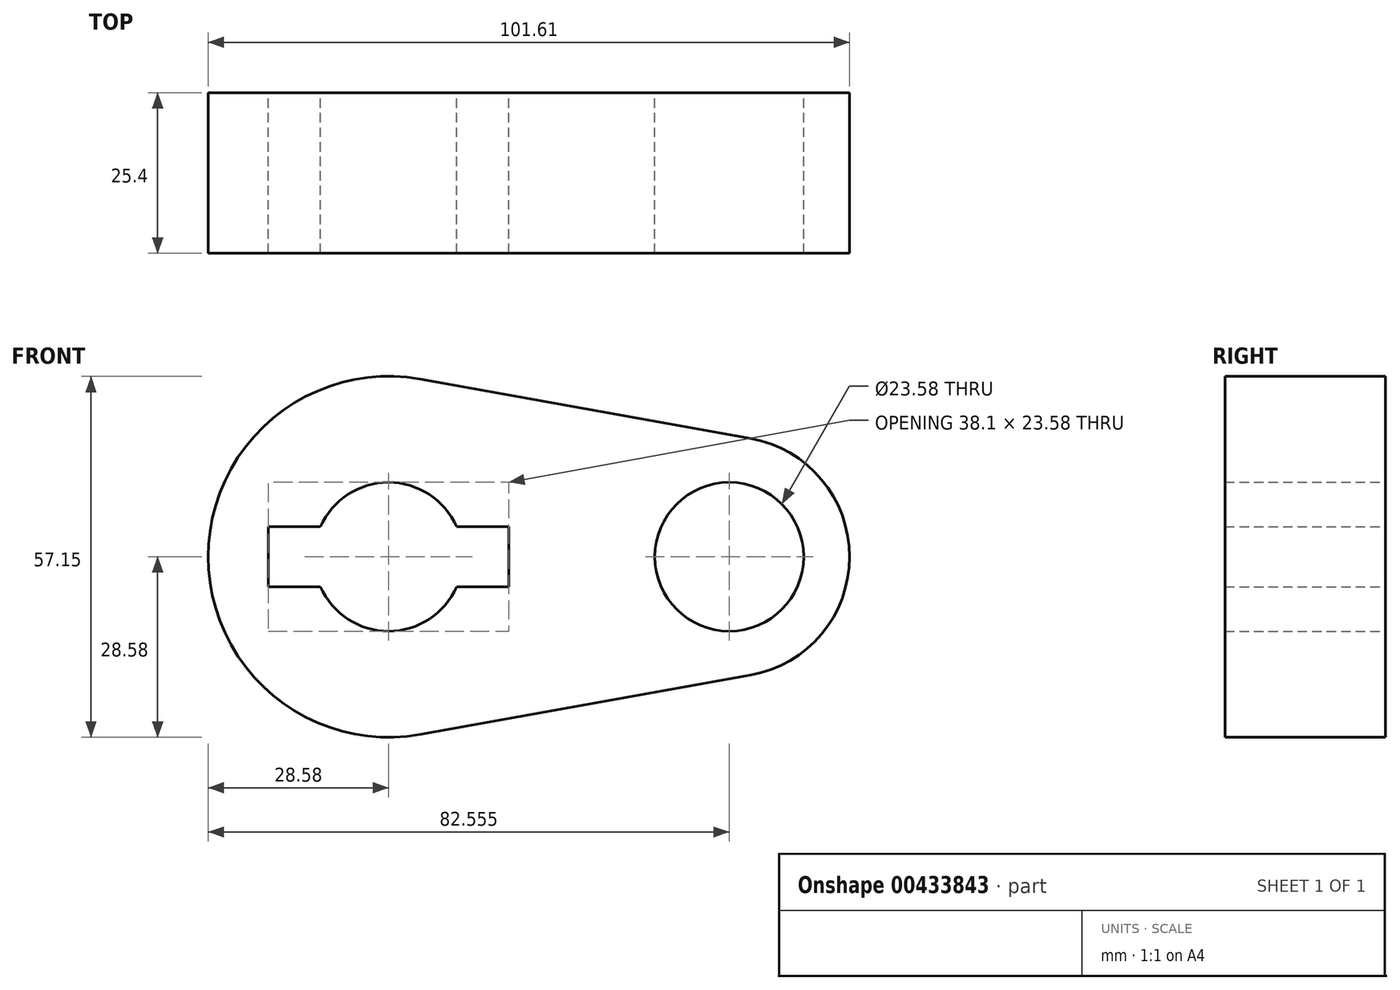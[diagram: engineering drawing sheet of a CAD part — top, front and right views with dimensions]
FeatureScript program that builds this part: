
annotation { "Feature Type Name" : "Feature", "Feature Type Description" : "" }
export const myFeature = defineFeature(function(context is Context, id is Id, definition is map)
    precondition{}
    {
        {
            var Q0;
            Q0=qCreatedBy(makeId("Front.planeOp"),FACE);
            var sketch = newSketch(context, id + "F0", { "sketchPlane" : qUnion([Q0])});
            skCircle(sketch, "E0", {"center": v(0, 0) * mm, "radius": 28.58 * mm});
            skCircle(sketch, "E1", {"center": v(53.98, 0) * mm, "radius": 19.05 * mm});
            skLineSegment(sketch, "E2", {"start": v(5.04, 28.13) * mm, "end": v(57.34, 18.75) * mm});
            skLineSegment(sketch, "E3", {"start": v(5.04, -28.13) * mm, "end": v(57.34, -18.75) * mm});
            skCircle(sketch, "E4", {"center": v(0, 0) * mm, "radius": 11.79 * mm});
            skCircle(sketch, "E5", {"center": v(53.98, 0) * mm, "radius": 11.79 * mm});
            skLineSegment(sketch, "E6.bottom", {"start": v(19.05, -4.76) * mm, "end": v(-19.05, -4.76) * mm});
            skLineSegment(sketch, "E6.top", {"start": v(19.05, 4.76) * mm, "end": v(-19.05, 4.76) * mm});
            skLineSegment(sketch, "E6.left", {"start": v(19.05, -4.76) * mm, "end": v(19.05, 4.76) * mm});
            skLineSegment(sketch, "E6.right", {"start": v(-19.05, -4.76) * mm, "end": v(-19.05, 4.76) * mm});
            skSolve(sketch);
        }
        {
            var Q0;
            Q0 = qSketchRegion(id + "F0", true);
            extrude(context, id + "F1", {"entities" : qUnion([Q0]), "depth" : 25.4 * mm});
        }
    });
